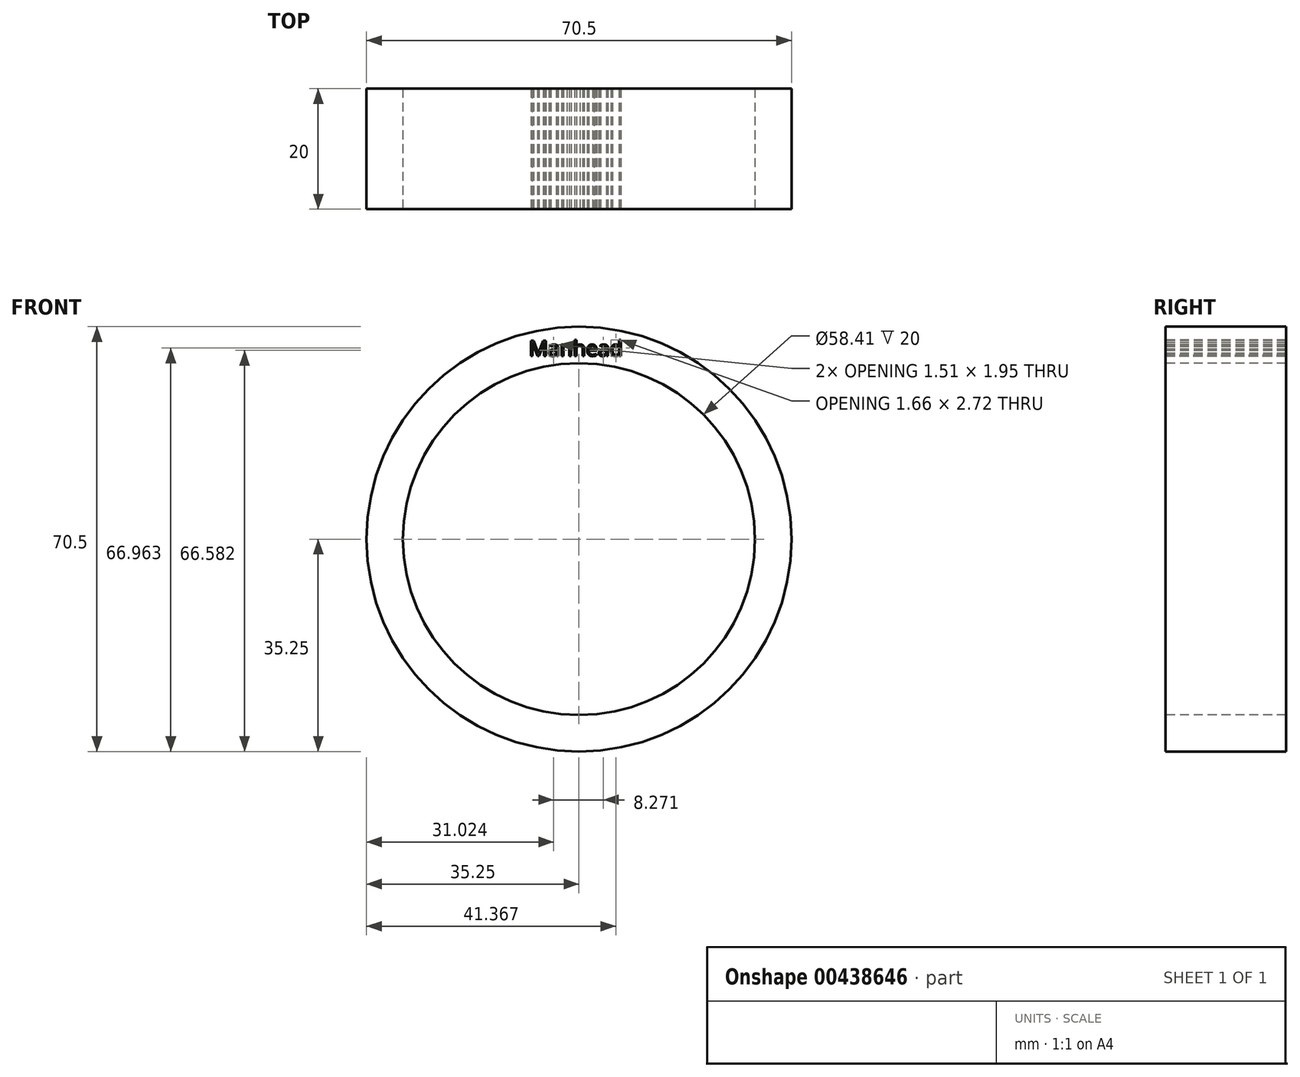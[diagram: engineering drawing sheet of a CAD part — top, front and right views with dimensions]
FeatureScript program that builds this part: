
annotation { "Feature Type Name" : "Feature", "Feature Type Description" : "" }
export const myFeature = defineFeature(function(context is Context, id is Id, definition is map)
    precondition{}
    {
        {
            var Q0;
            Q0=qCreatedBy(makeId("Front.planeOp"),FACE);
            var sketch = newSketch(context, id + "F0", { "sketchPlane" : qUnion([Q0])});
            skCircle(sketch, "E0", {"center": v(0, 0) * mm, "radius": 35.25 * mm});
            skSolve(sketch);
        }
        {
            var Q0;
            Q0 = qSketchRegion(id + "F0", true);
            extrude(context, id + "F1", {"entities" : qUnion([Q0]), "oppositeDirection" : true, "depth" : 20 * mm});
        }
        {
            var Q0;
            Q0=makeQuery(id+"F1.opExtrude","CAP_FACE",FACE,{"disambiguationData":[OSD([sQuery(id+"F0.wireOp",EDGE,"E0")])],"isStart":true});
            var sketch = newSketch(context, id + "F2", { "sketchPlane" : qUnion([Q0])});
            skCircle(sketch, "E1", {"center": v(0, 0) * mm, "radius": 29.2 * mm});
            skSolve(sketch);
        }
        {
            var Q0;
            Q0=makeQuery(id+"F2.imprint","IMPRINT",FACE,{"disambiguationData":[TD([[makeQuery(id+"F2.imprint","IMPRINT",EDGE,{"derivedFrom":sQuery(id+"F2.wireOp",EDGE,"E1")}),1.0]])]});
            extrude(context, id + "F3", {"entities" : qUnion([Q0]), "operationType" : NewBodyOperationType.REMOVE, "endBound" : BoundingType.THROUGH_ALL, "oppositeDirection" : true, "depth" : 25.4 * mm});
        }
        {
            var Q0;
            Q0=qCreatedBy(makeId("Front.planeOp"),FACE);
            var sketch = newSketch(context, id + "F4", { "sketchPlane" : qUnion([Q0])});
            skText(sketch, "E2", { "text": "Manhead\n", "fontName": "OpenSans-Regular.ttf"});
            const initialGuessF4  = {"E2": [-0.00833, 0.03039, 1, 0, 0.00254]};
            skSetInitialGuess(sketch, initialGuessF4);
            skSolve(sketch);
        }
        {
            var Q0;
            Q0 = qSketchRegion(id + "F4", true);
            extrude(context, id + "F5", {"entities" : qUnion([Q0]), "operationType" : NewBodyOperationType.REMOVE, "endBound" : BoundingType.THROUGH_ALL, "oppositeDirection" : true, "depth" : 25.4 * mm});
        }
    });
